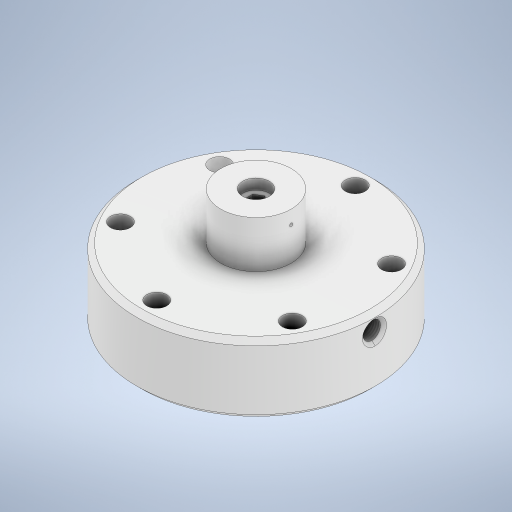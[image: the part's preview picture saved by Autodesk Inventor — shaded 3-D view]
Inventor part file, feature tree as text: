
AUTODESK INVENTOR PART (.ipt)
format: ipt  version: 2023 (Build 270158030, 158C)  size: 437,760 bytes
history: native  units: in
note: dims shown in document units (in); Inventor stores cm internally (conversion verified against a paired STEP export)
features: sketch x13, extrude x4, hole x4, plane x4, chamfer x2, sweep x2, pattern_circular x1, other x1, projected_geometry x1
ambient origin geometry x8: Origin, YZ Plane, XZ Plane, XY Plane, X Axis, Y Axis, Z Axis, Center Point
bodies: Solid1 (feature_tree)
feature tree (32):
  extrude  "Main Body"  Depth=1.75in TaperAngle=0.0deg
  hole  "M5 Bolt"  [1 undecoded]
  pattern_circular  "Circular Pattern1"  Count=6 Angle=360.0deg
  other  "Membrane Cutout"
  chamfer  "Chamfer1"  Distance=0.125in Angle=45.0deg
  sketch  "Sketch5"  dims[d33=0.125in d45=0.1in]
  plane  "Work Plane1"
  sweep  "Sweep2"
  plane  "Work Plane4"
  hole  "Hole7"  [1 undecoded]
  extrude  "Extrusion2"  Depth=0.9449in
  extrude  "Extrusion3"  TaperAngle=0.0deg  [1 undecoded]
  extrude  "Extrusion4"  Depth=0.0246in
  plane  "Work Plane2"
  hole  "Hole5"  [1 undecoded]
  sketch  "Sketch12"  dims[d73=0.3937in d74=0.0in d75=0.0in]
  plane  "Work Plane3"
  sweep  "Sweep3"
  hole  "Hole6"  [1 undecoded]
  chamfer  "Chamfer2"  Distance=0.5in
  sketch  "Sketch1"  dims[d0=6.0in d1=1.75in d2=0.0in]
  sketch  "Sketch2"  dims[d3=0.22in d4=0.75in d5=0.5in d6=0.75in d7=0.5635in d8=0.9798in d9=0.0in d10=2.5in d11=2.3622in d12=360.0deg]
  sketch  "Sketch3"  dims[d17=360.0deg d30=0.125in d31=0.125in d32=45.0deg]
  sketch  "Sketch7"  dims[d46=0.0in d47=0.0in d57=0.56in]
  sketch  "Sketch10"  dims[d59=1.1811in d60=0.0in]
  sketch  "Sketch11"  dims[d61=0.0787in d62=0.2362in d63=0.1181in d64=0.0787in d65=90.0deg d66=0.6167in d67=0.8108in d72=0.9449in]
  projected_geometry  "Projected Loop1"
  sketch  "Sketch13"  dims[d76=0.3937in]
  sketch  "Sketch14"  dims[d77=0.422in d78=0.3389in d79=0.2756in d80=0.0787in d81=90.0deg d82=0.6167in d83=0.8108in d84=0.0246in d85=0.426in d86=1.7717in]
  sketch  "Sketch15"  dims[d87=0.375in d88=0.2756in d89=0.0in]
  sketch  "Sketch16"  dims[d90=0.1083in d91=0.6689in]
  sketch  "Sketch18"  dims[d92=0.2638in d93=0.0in d94=0.3445in d95=0.5in d96=0.8in d98=2.6772in d99=0.7874in d100=0.25in d101=0.2362in d102=0.1575in d103=0.0787in d104=90.0deg d105=0.26in d106=0.8108in d107=2.25in d108=0.5in d109=0.25in d110=0.0787in d111=0.0787in d112=45.0deg]
note: 5 required parameter values undecoded (feature->parameter linkage not recoverable at this tier; creation-order binding heuristic only, values carry confidence <= 0.55)
